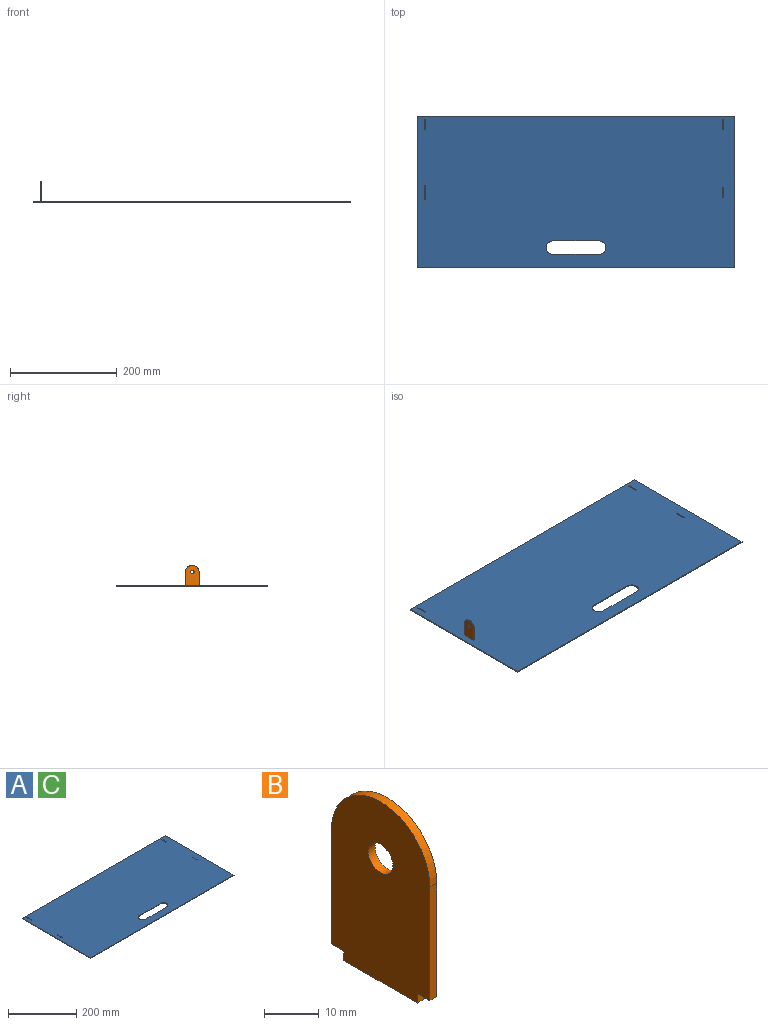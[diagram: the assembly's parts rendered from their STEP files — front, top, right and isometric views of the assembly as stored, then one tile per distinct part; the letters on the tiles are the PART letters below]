
ASSEMBLY  parts=3 mates=1
PART A: 26 faces, bbox 594.4x284.5x1.8 mm
  f0: plane 2.11x1.8mm, normal (0,1,0), area 3.8mm2, adj f1,f23,f24,f25
  f1: plane 19.05x1.8mm, normal (-1,0,0), area 34.2mm2, adj f0,f2,f24,f25
  f2: plane 2.11x1.8mm, normal (0,-1,0), area 3.8mm2, adj f1,f23,f24,f25
  f3: plane 2.11x1.8mm, normal (0,1,0), area 3.8mm2, adj f4,f22,f24,f25
  f4: plane 19.05x1.8mm, normal (-1,0,0), area 34.2mm2, adj f3,f5,f24,f25
  f5: plane 2.11x1.8mm, normal (0,-1,0), area 3.8mm2, adj f4,f22,f24,f25
  f6: cylinder r=12.7mm len=25.4mm, axis (0,0,1), area 71.6mm2, adj f7,f21,f24,f25
  f7: plane 86.36x1.8mm, normal (0,-1,0), area 155.1mm2, adj f6,f8,f24,f25
  f8: cylinder r=12.7mm len=25.4mm, axis (0,0,1), area 71.6mm2, adj f7,f21,f24,f25
  f9: plane 284.48x1.8mm, normal (1,0,0), area 510.9mm2, adj f10,f20,f24,f25
  f10: plane 594.36x1.8mm, normal (0,-1,0), area 1067.3mm2, adj f9,f11,f24,f25
  f11: plane 284.48x1.8mm, normal (-1,0,0), area 510.9mm2, adj f10,f20,f24,f25
  f12: plane 2.11x1.8mm, normal (0,1,0), area 3.8mm2, adj f13,f19,f24,f25
  f13: plane 19.05x1.8mm, normal (-1,0,0), area 34.2mm2, adj f12,f14,f24,f25
  f14: plane 2.11x1.8mm, normal (0,-1,0), area 3.8mm2, adj f13,f19,f24,f25
  f15: plane 2.11x1.8mm, normal (0,1,0), area 3.8mm2, adj f16,f18,f24,f25
  f16: plane 19.05x1.8mm, normal (-1,0,0), area 34.2mm2, adj f15,f17,f24,f25
  f17: plane 2.11x1.8mm, normal (0,-1,0), area 3.8mm2, adj f16,f18,f24,f25
  f18: plane 19.05x1.8mm, normal (1,0,0), area 34.2mm2, adj f15,f17,f24,f25
  f19: plane 19.05x1.8mm, normal (1,0,0), area 34.2mm2, adj f12,f14,f24,f25
  f20: plane 594.36x1.8mm, normal (0,1,0), area 1067.3mm2, adj f9,f11,f24,f25
  f21: plane 86.36x1.8mm, normal (0,1,0), area 155.1mm2, adj f6,f8,f24,f25
  f22: plane 19.05x1.8mm, normal (1,0,0), area 34.2mm2, adj f3,f5,f24,f25
  f23: plane 19.05x1.8mm, normal (1,0,0), area 34.2mm2, adj f0,f2,f24,f25
  f24: plane 594.36x284.48mm, normal (0,0,-1), area 166222.6mm2, adj f0,f1,f2,f3,f4,f5,f6,f7
  f25: plane 594.36x284.48mm, normal (0,0,1), area 166222.6mm2, adj f0,f1,f2,f3,f4,f5,f6,f7
PART B: 11 faces, bbox 1.8x25.4x40.2 mm
  f0: plane 25.4x1.8mm, normal (0,1,0), area 45.6mm2, adj f1,f8,f9,f10
  f1: plane 3.18x1.8mm, normal (0,0,-1), area 5.7mm2, adj f0,f2,f9,f10
  f2: plane 2.11x1.8mm, normal (0,1,0), area 3.8mm2, adj f1,f3,f9,f10
  f3: plane 19.05x1.8mm, normal (0,0,-1), area 34.2mm2, adj f2,f4,f9,f10
  f4: plane 2.11x1.8mm, normal (0,-1,0), area 3.8mm2, adj f3,f5,f9,f10
  f5: plane 3.18x1.8mm, normal (0,0,-1), area 5.7mm2, adj f4,f6,f9,f10
  f6: plane 25.4x1.8mm, normal (0,-1,0), area 45.6mm2, adj f5,f8,f9,f10
  f7: cylinder r=3.17mm len=6.35mm, axis (1,0,0), area 35.8mm2, adj f9,f10
  f8: cylinder r=12.7mm len=25.4mm, axis (1,0,0), area 71.6mm2, adj f0,f6,f9,f10
  f9: plane 40.21x25.4mm, normal (-1,0,0), area 907mm2, adj f0,f1,f2,f3,f4,f5,f6,f7
  f10: plane 40.21x25.4mm, normal (1,0,0), area 907mm2, adj f0,f1,f2,f3,f4,f5,f6,f7
PART C: same geometry as A
PLACE A at identity
PLACE B t=(13.01,128.9,2.11)mm
PLACE C at identity
MATE fastened B.f3 <-> C.f24  axis (0,0,1) through (14.81,151.13,0)mm
